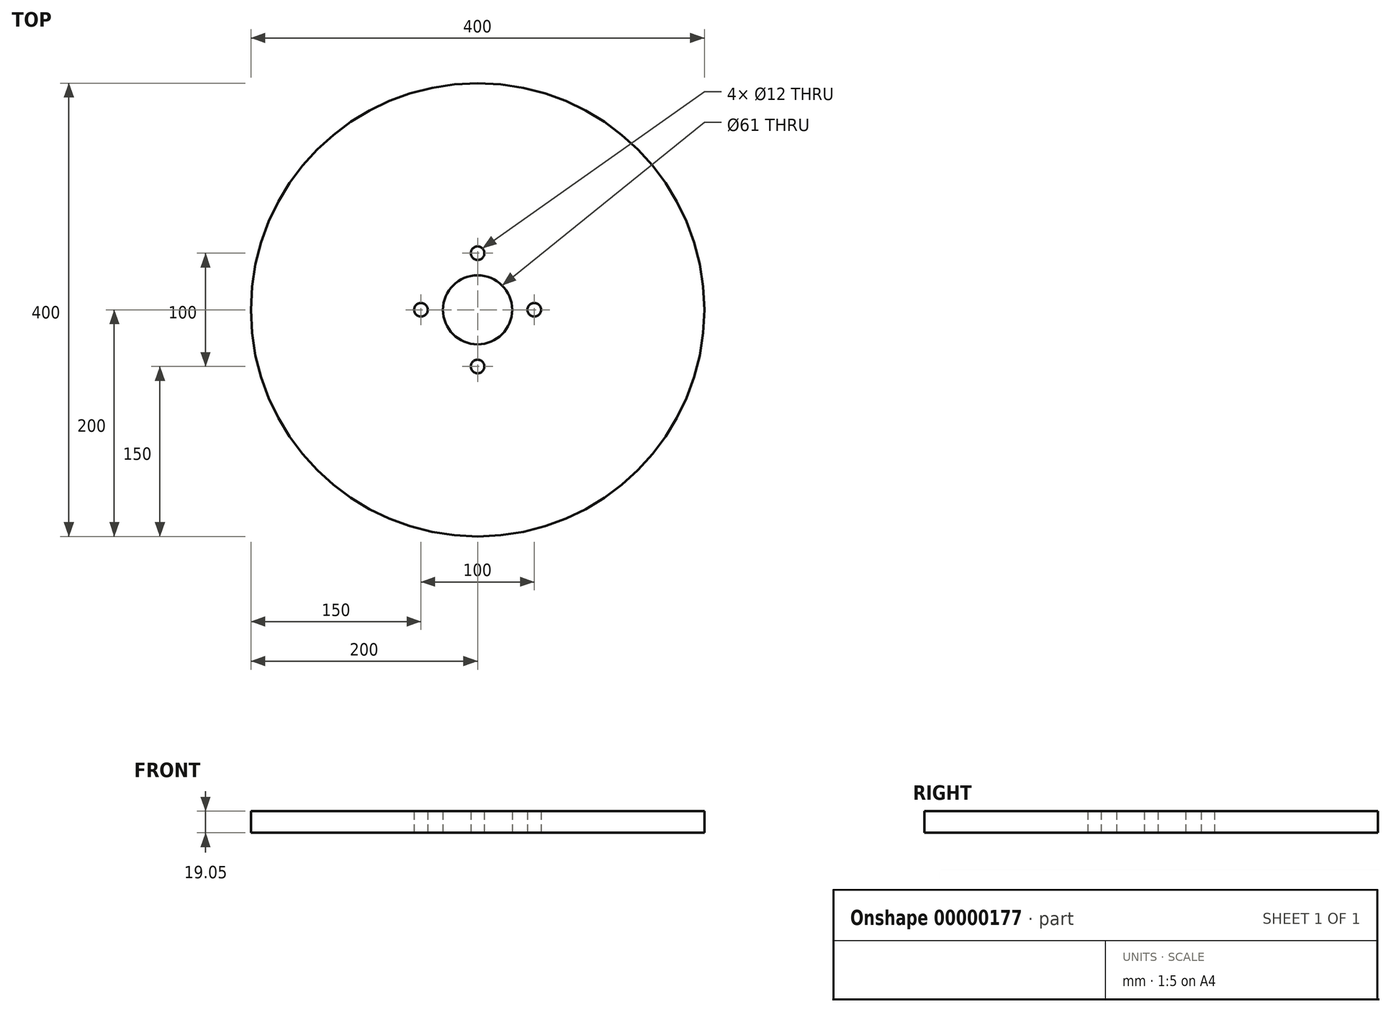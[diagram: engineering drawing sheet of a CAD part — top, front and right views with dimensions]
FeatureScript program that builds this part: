
annotation { "Feature Type Name" : "Feature", "Feature Type Description" : "" }
export const myFeature = defineFeature(function(context is Context, id is Id, definition is map)
    precondition{}
    {
        {
            var Q0;
            Q0=qCreatedBy(makeId("Top.planeOp"),FACE);
            var sketch = newSketch(context, id + "F0", { "sketchPlane" : qUnion([Q0])});
            skCircle(sketch, "E0", {"center": v(0, 0) * mm, "radius": 200 * mm});
            skSolve(sketch);
        }
        {
            var Q0;
            Q0=makeQuery(id+"F0.imprint","IMPRINT",FACE,{"disambiguationData":[TD([[makeQuery(id+"F0.imprint","IMPRINT",EDGE,{"derivedFrom":sQuery(id+"F0.wireOp",EDGE,"E0")}),1.0]])]});
            extrude(context, id + "F1", {"entities" : qUnion([Q0]), "depth" : 19.05 * mm});
        }
        {
            var Q0;
            Q0=qCreatedBy(makeId("Top.planeOp"),FACE);
            var sketch = newSketch(context, id + "F2", { "sketchPlane" : qUnion([Q0])});
            skCircle(sketch, "E1", {"center": v(0, 0) * mm, "radius": 30.5 * mm});
            skCircle(sketch, "E2", {"center": v(0, 0) * mm, "radius": 50 * mm, "construction": true});
            skCircle(sketch, "E3", {"center": v(0, 50) * mm, "radius": 6 * mm});
            skCircle(sketch, "E4", {"center": v(0, -50) * mm, "radius": 6 * mm});
            skCircle(sketch, "E5", {"center": v(-50, 0) * mm, "radius": 6 * mm});
            skCircle(sketch, "E6", {"center": v(50, 0) * mm, "radius": 6 * mm});
            skSolve(sketch);
        }
        {
            var Q0;
            Q0=makeQuery(id+"F2.imprint","IMPRINT",FACE,{"disambiguationData":[TD([[makeQuery(id+"F2.imprint","IMPRINT",EDGE,{"derivedFrom":sQuery(id+"F2.wireOp",EDGE,"E1")}),1.0]])]});
            var Q1;
            Q1=makeQuery(id+"F2.imprint","IMPRINT",FACE,{"disambiguationData":[TD([[makeQuery(id+"F2.imprint","IMPRINT",EDGE,{"derivedFrom":sQuery(id+"F2.wireOp",EDGE,"E5")}),1.0]])]});
            var Q2;
            Q2=makeQuery(id+"F2.imprint","IMPRINT",FACE,{"disambiguationData":[TD([[makeQuery(id+"F2.imprint","IMPRINT",EDGE,{"derivedFrom":sQuery(id+"F2.wireOp",EDGE,"E3")}),1.0]])]});
            var Q3;
            Q3=makeQuery(id+"F2.imprint","IMPRINT",FACE,{"disambiguationData":[TD([[makeQuery(id+"F2.imprint","IMPRINT",EDGE,{"derivedFrom":sQuery(id+"F2.wireOp",EDGE,"E6")}),1.0]])]});
            var Q4;
            Q4=makeQuery(id+"F2.imprint","IMPRINT",FACE,{"disambiguationData":[TD([[makeQuery(id+"F2.imprint","IMPRINT",EDGE,{"derivedFrom":sQuery(id+"F2.wireOp",EDGE,"E4")}),1.0]])]});
            var Q5;
            Q5=makeQuery(id+"F1.opExtrude","CAP_FACE",FACE,{"disambiguationData":[OSD([sQuery(id+"F0.wireOp",EDGE,"E0")])],"isStart":false});
            extrude(context, id + "F3", {"entities" : qUnion([Q0, Q1, Q2, Q3, Q4]), "operationType" : NewBodyOperationType.REMOVE, "endBound" : BoundingType.UP_TO_SURFACE, "endBoundEntityFace" : qUnion([Q5]), "depth" : 19.05 * mm});
        }
    });
